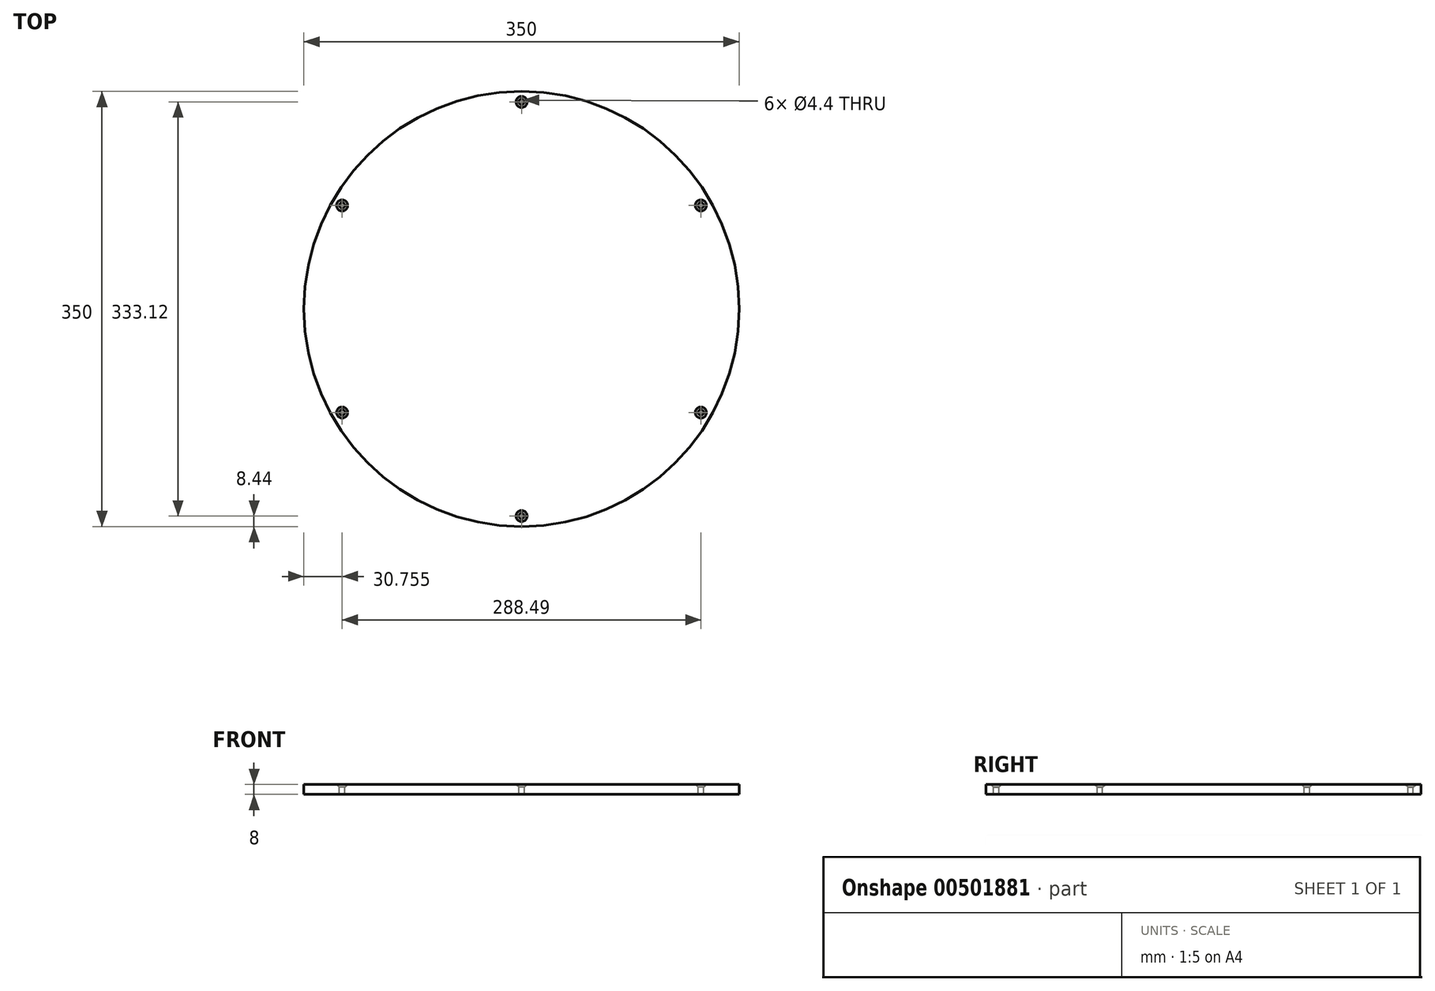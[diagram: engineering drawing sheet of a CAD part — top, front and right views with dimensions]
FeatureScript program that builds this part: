
annotation { "Feature Type Name" : "Feature", "Feature Type Description" : "" }
export const myFeature = defineFeature(function(context is Context, id is Id, definition is map)
    precondition{}
    {
        {
            var Q0;
            Q0=qCreatedBy(makeId("Top.planeOp"),FACE);
            var sketch = newSketch(context, id + "F0", { "sketchPlane" : qUnion([Q0])});
            skCircle(sketch, "E0", {"center": v(0, 0) * mm, "radius": 175 * mm});
            skCircle(sketch, "E1", {"center": v(0, 0) * mm, "radius": 166.56 * mm, "construction": true});
            skPoint(sketch, "E2", {"position": v(0, -166.56) * mm});
            skPoint(sketch, "E3.1.0", {"position": v(144.25, -83.28) * mm});
            skPoint(sketch, "E3.2.0", {"position": v(144.25, 83.28) * mm});
            skPoint(sketch, "E3.3.0", {"position": v(0, 166.56) * mm});
            skPoint(sketch, "E3.4.0", {"position": v(-144.25, 83.28) * mm});
            skPoint(sketch, "E3.5.0", {"position": v(-144.25, -83.28) * mm});
            skCircle(sketch, "E4", {"center": v(0, -166.56) * mm, "radius": 1.65 * mm});
            skCircle(sketch, "E5.1.0", {"center": v(-144.25, -83.28) * mm, "radius": 1.65 * mm});
            skCircle(sketch, "E5.2.0", {"center": v(-144.25, 83.28) * mm, "radius": 1.65 * mm});
            skLineSegment(sketch, "E5.anchor1", {"start": v(0, 0) * mm, "end": v(0, -166.56) * mm, "construction": true});
            skLineSegment(sketch, "E5.anchor2", {"start": v(0, 0) * mm, "end": v(144.25, -83.28) * mm, "construction": true});
            skCircle(sketch, "E6.1.3.0", {"center": v(0, 166.56) * mm, "radius": 1.65 * mm});
            skCircle(sketch, "E6.1.4.0", {"center": v(144.25, 83.28) * mm, "radius": 1.65 * mm});
            skCircle(sketch, "E6.1.5.0", {"center": v(144.25, -83.28) * mm, "radius": 1.65 * mm});
            skSolve(sketch);
        }
        {
            var Q0;
            Q0=makeQuery(id+"F0.imprint","IMPRINT",FACE,{"disambiguationData":[TD([[makeQuery(id+"F0.imprint","IMPRINT",EDGE,{"derivedFrom":sQuery(id+"F0.wireOp",EDGE,"E0")}),1.0]])]});
            extrude(context, id + "F1", {"entities" : qUnion([Q0]), "depth" : 8 * mm});
        }
        {
            var Q0;
            Q0=makeQuery(id+"F1.opExtrude","CAP_FACE",FACE,{"disambiguationData":[OSD([sQuery(id+"F0.wireOp",EDGE,"E0")])],"isStart":false});
            var sketch = newSketch(context, id + "F2", { "sketchPlane" : qUnion([Q0])});
            skCircle(sketch, "E7", {"center": v(0, 0) * mm, "radius": 166.56 * mm, "construction": true});
            skPoint(sketch, "E8", {"position": v(0, -166.56) * mm});
            skPoint(sketch, "E9.1.0", {"position": v(-144.25, -83.28) * mm});
            skPoint(sketch, "E9.2.0", {"position": v(-144.25, 83.28) * mm});
            skLineSegment(sketch, "E9.anchor1", {"start": v(0, 0) * mm, "end": v(0, -166.56) * mm, "construction": true});
            skLineSegment(sketch, "E9.anchor2", {"start": v(0, 0) * mm, "end": v(-144.25, 83.28) * mm, "construction": true});
            skPoint(sketch, "E10.MirrorP", {"position": v(144.25, -83.28) * mm});
            skPoint(sketch, "E11.MirrorP", {"position": v(144.25, 83.28) * mm});
            skPoint(sketch, "E12.MirrorP", {"position": v(0, 166.56) * mm});
            skSolve(sketch);
        }
        {
            var Q0;
            Q0=sQuery(id+"F2.wireOp",VERTEX,"E9.1.0");
            var Q1;
            Q1=sQuery(id+"F2.wireOp",VERTEX,"E9.2.0");
            var Q2;
            Q2=sQuery(id+"F2.wireOp",VERTEX,"E12.MirrorP");
            var Q3;
            Q3=sQuery(id+"F2.wireOp",VERTEX,"E11.MirrorP");
            var Q4;
            Q4=sQuery(id+"F2.wireOp",VERTEX,"E10.MirrorP");
            var Q5;
            Q5=sQuery(id+"F2.wireOp",VERTEX,"E8");
            var Q6;
            Q6=makeQuery(id+"F1.opExtrude","SWEPT_BODY",BODY,{"disambiguationData":[OSD([sQuery(id+"F0.wireOp",EDGE,"E0")])]});
            hole(context, id + "F3", {"style" : HoleStyle.C_SINK, "endStyle" : HoleEndStyle.THROUGH, "standardTappedOrClearance" : lookupTablePath({ "standard" : "ISO", "fit" : "Normal", "size" : "M4", "type" : "Clearance" }), "standardBlindInLast" : lookupTablePath({ "fit" : "Standard", "standard" : "ISO", "size" : "M4", "type" : "Clearance" }), "holeDiameter" : 4.4 * mm, "cSinkDiameter" : 8.96 * mm, "cSinkAngle" : 90 * degree, "majorDiameter" : 5 * mm, "isTappedThrough" : true, "tappedDepth" : 12 * mm, "tapClearance" : 3, "locations" : qUnion([Q0, Q1, Q2, Q3, Q4, Q5]), "scope" : qUnion([Q6])});
        }
    });
